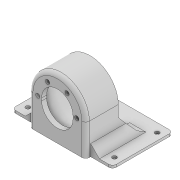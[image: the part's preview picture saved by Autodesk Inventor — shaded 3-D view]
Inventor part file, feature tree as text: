
AUTODESK INVENTOR PART (.ipt)
format: ipt  version: 2022 (Build 260153000, 153)  size: 224,256 bytes
history: native  units: mm
features: sketch x6, extrude x4, chamfer x3, hole x2, fillet x2, mirror x1
ambient origin geometry x8: Origin, YZ Plane, XZ Plane, XY Plane, X Axis, Y Axis, Z Axis, Center Point
bodies: Solid1 (feature_tree)
feature tree (18):
  extrude  "Extrusion1"  Depth=80.0mm
  extrude  "Extrusion2"  Depth=22.5mm
  extrude  "Extrusion3"  Depth=25.0mm
  hole  "Hole1"  [1 undecoded]
  extrude  "Extrusion4"  Depth=22.0mm
  mirror  "Mirror1"
  hole  "Hole2"  [1 undecoded]
  chamfer  "Chamfer1"  Distance=6.5mm
  chamfer  "Chamfer2"  Distance=14.0mm
  chamfer  "Chamfer3"  Distance=12.0mm
  fillet  "Fillet1"  Radius=3.0mm
  fillet  "Fillet2"  Radius=2.0mm
  sketch  "Sketch1"  dims[d0=48.0mm d1=80.0mm]
  sketch  "Sketch2"  dims[d2=2.0mm d3=0.0mm d5=22.5mm]
  sketch  "Sketch3"  dims[d6=2.0mm d7=25.0mm]
  sketch  "Sketch4"  dims[d9=4.0mm d10=0.0mm d11=38.0mm]
  sketch  "Sketch5"  dims[d12=22.0mm d13=0.0mm d14=31.0mm]
  sketch  "Sketch6"  dims[d15=60.0mm d17=360.0deg d19=3.4mm d20=6.0mm d21=4.0mm d22=2.0mm d23=90.0deg d24=8.0mm d25=20.594885mm d27=37.0mm d28=6.5mm d29=14.0mm d30=12.0mm d31=3.0mm d32=0.0mm d33=0.5mm d34=2.0mm d35=45.0deg d36=3.0mm d37=2.0mm d38=45.0deg d39=7.0mm d40=2.0mm d41=45.0deg d42=3.0mm d43=3.0mm d44=7.0mm d45=34.0mm d46=69.0mm d47=3.4mm d48=6.0mm d49=4.0mm d50=2.0mm d51=90.0deg d52=8.0mm d53=20.594885mm]
note: 2 required parameter values undecoded (feature->parameter linkage not recoverable at this tier; creation-order binding heuristic only, values carry confidence <= 0.55)
